# Revit family: Shower-Showerhead-KOHLER-Modern_Life-K-27731IN.rfa_
name_source: partatom
category: Plumbing Fixtures
units: mm (PartAtom-declared; Revit-internal decimal feet)

## family parameters
Cut with Voids When Loaded = No
Host = Face
Maintain Annotation Orientation = No
OmniClass Number = 23.31.17.00
OmniClass Title = Showers
Part Type = Normal
Room Calculation Point = No
Round Connector Dimension = Use Diameter
Shared = No

## types (5) — shared parameters
ADA Compliant = No
Assembly Code = D2010700
CW Connection = No
Cold Water Inlet = Cold Water Inlet
Date Modified = 07/27/2024
Default Elevation = 42"
Description = Single function rainpanel
Drain Included = No
Flow Rate = 0 GPM
HW Connection = Yes
Height = 2 7/16"
Hot Water Inlet = Tempered Water Inlet
Length = 13 3/16"
Manufacturer = Kohler Co.
Master Format 2014 = 22 42 23
Master Format 2014 Name = Residential Showers
Material = Plastic
Pressure = 0.00 psi
Product Name = Modern Life
Product Page URL = https://www.kohler.co.in
URL = https://www.kohler.co.in
Vent Connection = No
Waste Connection = No
Waste Water Outlet = Waste Water Outlet
WaterSense Certified = No
Width = 8 11/16"

## per-type parameters (varying)
| type | Finish | Model | Secondary Finish | Type |
| CP-Polished Chrome | Kohler-Plastic-CP-Polished_Chrome | K-27731IN-CP | Kohler-Plastic-0-White | 1 |
| BL-Matte Black | Kohler-Plastic-BL-Matte_Black | K-27731IN-BL | Plastic-Pantone-425C | 2 |
| AF-Vibrant French Gold | KOHLER-Plastic-AF-Vibrant_French_Gold | K-27731IN-AF | Kohler-Plastic-0-White | 3 |
| BV-Brushed Bronze | Kohler-Plastic-BV-Brushed_Bronze | K-27731IN-BV | Kohler-Plastic-0-White | 4 |
| RGD-Polished Rose Gold | Kohler-Plastic-RGD-Polished_Rose_Gold | K-27731IN-RGD | Kohler-Plastic-0-White | 5 |

## geometry (parser evidence)
native form markers: Sweep x6
no freeform markers — native parametric forms only
